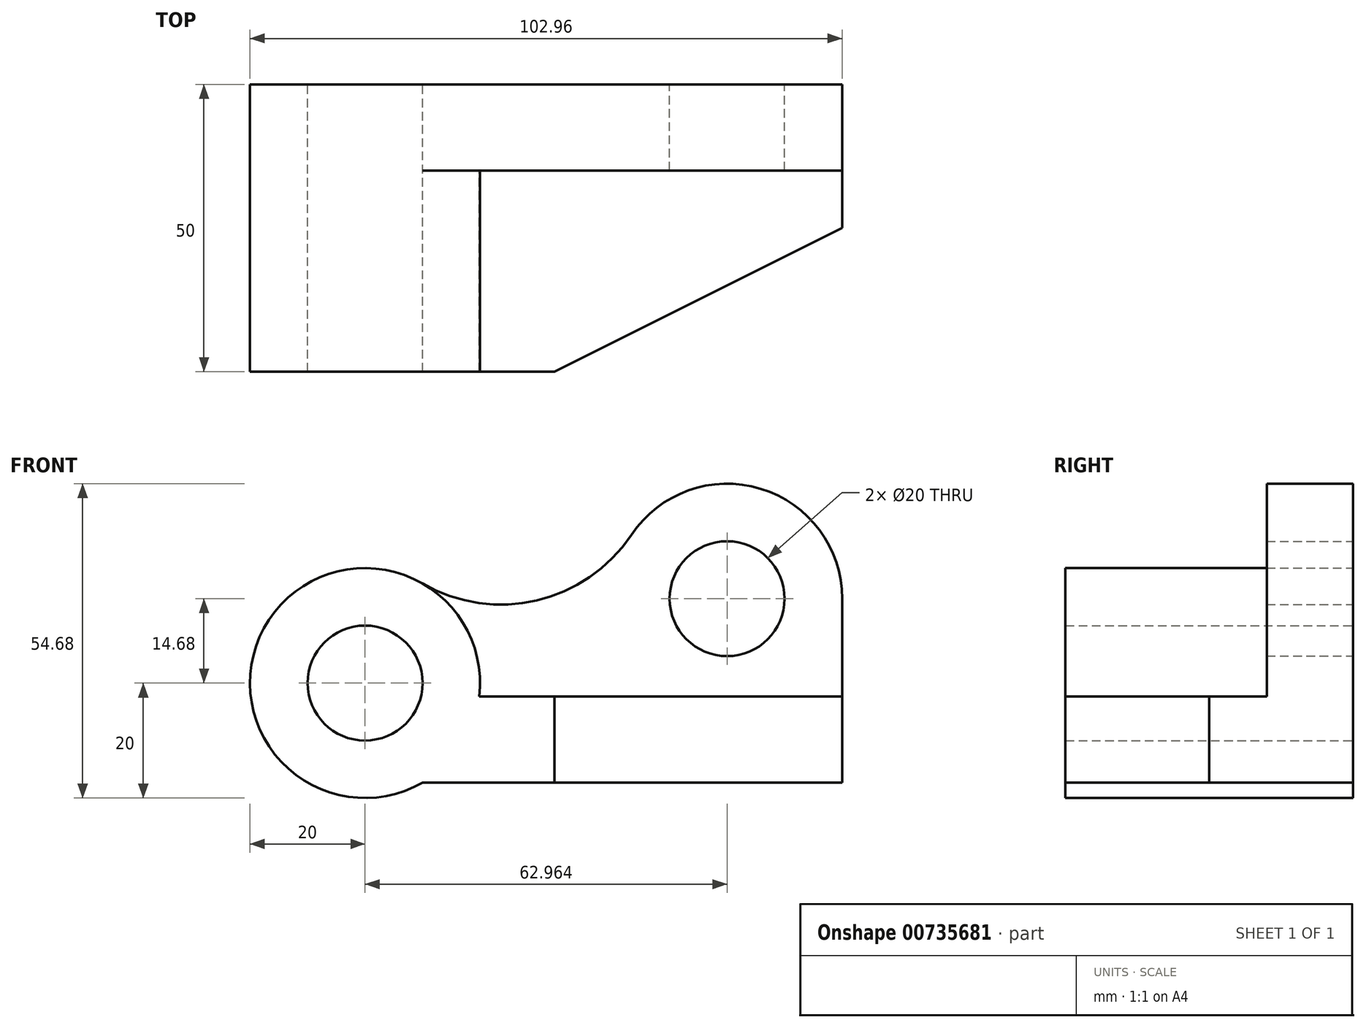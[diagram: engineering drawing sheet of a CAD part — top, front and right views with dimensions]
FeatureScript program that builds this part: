
annotation { "Feature Type Name" : "Feature", "Feature Type Description" : "" }
export const myFeature = defineFeature(function(context is Context, id is Id, definition is map)
    precondition{}
    {
        {
            var Q0;
            Q0=qCreatedBy(makeId("Front.planeOp"),FACE);
            var sketch = newSketch(context, id + "F0", { "sketchPlane" : qUnion([Q0])});
            skCircle(sketch, "E0", {"center": v(0, 0) * mm, "radius": 10 * mm});
            skArc(sketch, "E1", {"start": v(10, 17.32) * mm, "mid": v(-20, 0) * mm, "end": v(10, -17.32) * mm});
            skArc(sketch, "E2", {"start": v(10, 17.32) * mm, "mid": v(29.84, 14.38) * mm, "end": v(46.34, 25.8) * mm});
            skCircle(sketch, "E3", {"center": v(62.96, 14.68) * mm, "radius": 10 * mm});
            skArc(sketch, "E4", {"start": v(82.96, 14.68) * mm, "mid": v(68.77, 33.82) * mm, "end": v(46.34, 25.8) * mm});
            skLineSegment(sketch, "E5", {"start": v(82.96, 14.68) * mm, "end": v(82.96, -17.32) * mm});
            skLineSegment(sketch, "E6", {"start": v(82.96, -17.32) * mm, "end": v(10, -17.32) * mm});
            skLineSegment(sketch, "E7", {"start": v(0, 0) * mm, "end": v(10, 17.32) * mm});
            skSolve(sketch);
        }
        {
            var Q0;
            Q0=makeQuery(id+"F0.imprint","IMPRINT",FACE,{"disambiguationData":[TD([[makeQuery(id+"F0.imprint","IMPRINT",EDGE,{"derivedFrom":sQuery(id+"F0.wireOp",EDGE,"E0")}),-1.0]])]});
            extrude(context, id + "F1", {"entities" : qUnion([Q0]), "depth" : 15 * mm, "offsetDistance" : 25 * mm});
        }
        {
            var Q0;
            Q0=makeQuery(id+"F1.opExtrude","CAP_FACE",FACE,{"disambiguationData":[OSD([sQuery(id+"F0.wireOp",EDGE,"E0"),sQuery(id+"F0.wireOp",EDGE,"E1"),sQuery(id+"F0.wireOp",EDGE,"E2"),sQuery(id+"F0.wireOp",EDGE,"E3"),sQuery(id+"F0.wireOp",EDGE,"E4"),sQuery(id+"F0.wireOp",EDGE,"E5"),sQuery(id+"F0.wireOp",EDGE,"E6")])],"isStart":false});
            var sketch = newSketch(context, id + "F2", { "sketchPlane" : qUnion([Q0])});
            skCircle(sketch, "E8", {"center": v(0, 0) * mm, "radius": 20 * mm});
            skCircle(sketch, "E9", {"center": v(0, 0) * mm, "radius": 10 * mm});
            skSolve(sketch);
        }
        {
            var Q0;
            Q0=makeQuery(id+"F2.imprint","IMPRINT",FACE,{"disambiguationData":[TD([[makeQuery(id+"F2.imprint","IMPRINT",EDGE,{"derivedFrom":sQuery(id+"F2.wireOp",EDGE,"E9")}),-1.0]])]});
            extrude(context, id + "F3", {"entities" : qUnion([Q0]), "operationType" : NewBodyOperationType.ADD, "depth" : 35 * mm, "offsetDistance" : 25 * mm});
        }
        {
            var Q0;
            Q0=makeQuery(id+"F1.opExtrude","CAP_FACE",FACE,{"disambiguationData":[OSD([sQuery(id+"F0.wireOp",EDGE,"E0"),sQuery(id+"F0.wireOp",EDGE,"E1"),sQuery(id+"F0.wireOp",EDGE,"E2"),sQuery(id+"F0.wireOp",EDGE,"E3"),sQuery(id+"F0.wireOp",EDGE,"E4"),sQuery(id+"F0.wireOp",EDGE,"E5"),sQuery(id+"F0.wireOp",EDGE,"E6")])],"isStart":false});
            var sketch = newSketch(context, id + "F4", { "sketchPlane" : qUnion([Q0])});
            skLineSegment(sketch, "E10.bottom", {"start": v(82.96, -17.32) * mm, "end": v(10, -17.32) * mm});
            skLineSegment(sketch, "E10.top", {"start": v(82.96, -2.32) * mm, "end": v(19.86, -2.32) * mm});
            skLineSegment(sketch, "E10.left", {"start": v(82.96, -17.32) * mm, "end": v(82.96, -2.32) * mm});
            skArc(sketch, "E11", {"start": v(10, -17.32) * mm, "mid": v(16.71, -10.99) * mm, "end": v(19.86, -2.32) * mm});
            skSolve(sketch);
        }
        {
            var Q0;
            Q0 = qSketchRegion(id + "F4", true);
            extrude(context, id + "F5", {"entities" : qUnion([Q0]), "operationType" : NewBodyOperationType.ADD, "depth" : 35 * mm, "offsetDistance" : 25 * mm});
        }
        {
            var Q0;
            Q0=makeQuery(id+"F5.opExtrude","SWEPT_FACE",FACE,{"disambiguationData":[OSD([sQuery(id+"F4.wireOp",EDGE,"E10.top")])]});
            var sketch = newSketch(context, id + "F6", { "sketchPlane" : qUnion([Q0])});
            skLineSegment(sketch, "E12", {"start": v(82.96, -15) * mm, "end": v(82.96, -25) * mm});
            skLineSegment(sketch, "E13", {"start": v(82.96, -50) * mm, "end": v(32.96, -50) * mm});
            skLineSegment(sketch, "E14", {"start": v(32.96, -50) * mm, "end": v(82.96, -25) * mm});
            skLineSegment(sketch, "E15", {"start": v(82.96, -50) * mm, "end": v(82.96, -25) * mm});
            skSolve(sketch);
        }
        {
            var Q0;
            Q0=makeQuery(id+"F6.imprint","IMPRINT",FACE,{"disambiguationData":[TD([[makeQuery(id+"F6.imprint","IMPRINT",EDGE,{"derivedFrom":sQuery(id+"F6.wireOp",EDGE,"E13")}),-1.0]])]});
            extrude(context, id + "F7", {"entities" : qUnion([Q0]), "operationType" : NewBodyOperationType.REMOVE, "endBound" : BoundingType.UP_TO_NEXT, "oppositeDirection" : true, "depth" : 25 * mm, "offsetDistance" : 25 * mm});
        }
    });
